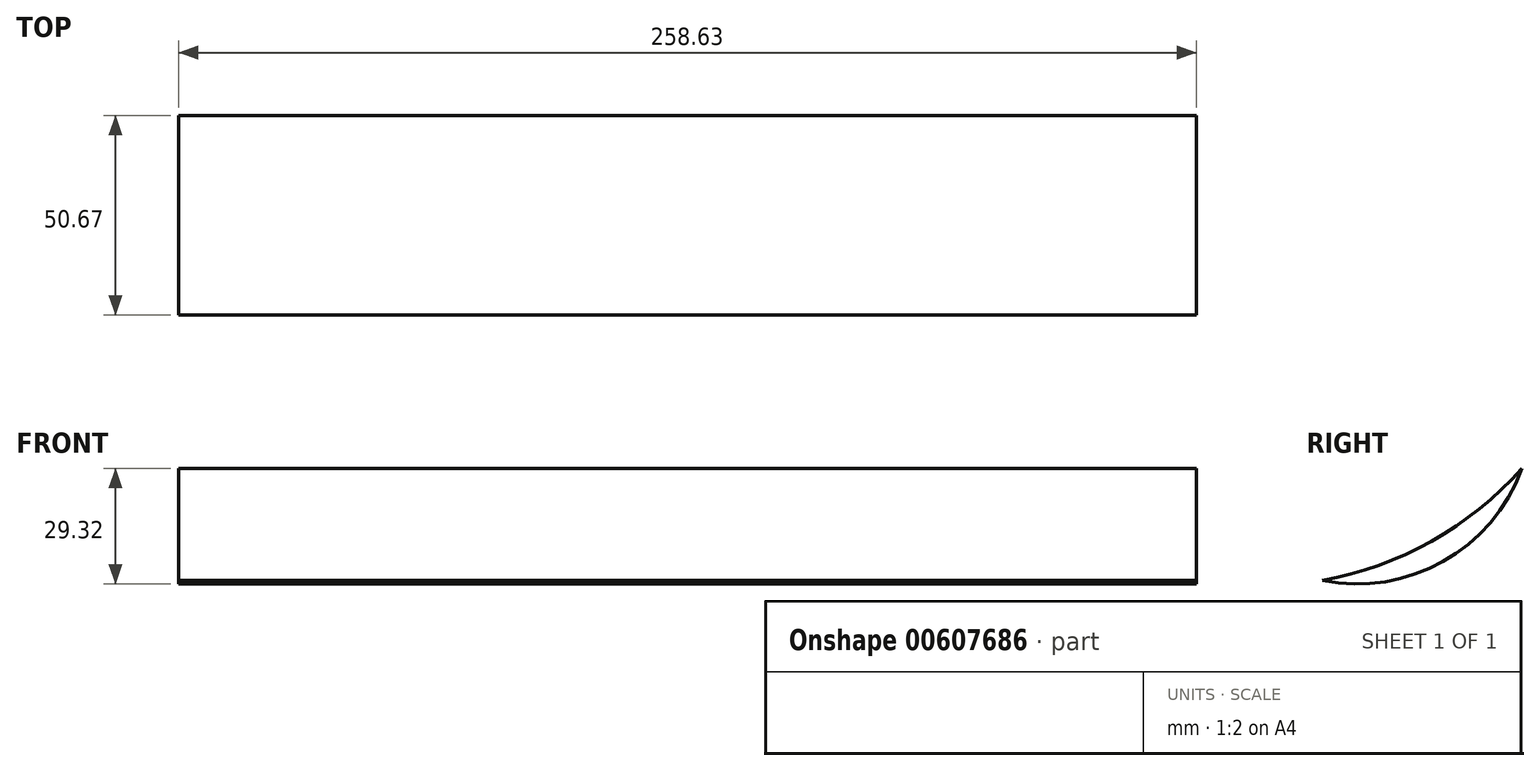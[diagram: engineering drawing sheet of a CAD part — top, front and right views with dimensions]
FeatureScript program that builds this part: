
annotation { "Feature Type Name" : "Feature", "Feature Type Description" : "" }
export const myFeature = defineFeature(function(context is Context, id is Id, definition is map)
    precondition{}
    {
        {
            var Q0;
            Q0=qCreatedBy(makeId("Right.planeOp"),FACE);
            var sketch = newSketch(context, id + "F0", { "sketchPlane" : qUnion([Q0])});
            skArc(sketch, "E0", {"start": v(0, 0) * mm, "mid": v(27.72, 9.96) * mm, "end": v(50.67, 28.42) * mm});
            skArc(sketch, "E1", {"start": v(0, 0) * mm, "mid": v(30.63, 4.78) * mm, "end": v(50.67, 28.42) * mm});
            skSolve(sketch);
        }
        {
            var Q0;
            Q0=makeQuery(id+"F0.imprint","IMPRINT",FACE,{"disambiguationData":[TD([[makeQuery(id+"F0.imprint","IMPRINT",EDGE,{"derivedFrom":sQuery(id+"F0.wireOp",EDGE,"E0")}),-1.0]])]});
            extrude(context, id + "F1", {"entities" : qUnion([Q0]), "depth" : 258.63 * mm, "offsetDistance" : 25.4 * mm});
        }
    });
